# Revit family: MI-XHUB
name_source: partatom
category: Pipe Accessories
revit_build: Autodesk Revit 2018 (Build: 20170223_1515(x64)
units: mm (PartAtom-declared; Revit-internal decimal feet)

## family parameters
Always vertical = Yes
Cut with Voids When Loaded = No
Part Type = Valve - Breaks Into
Round Connector Dimension = Use Diameter
Shared = No
Work Plane-Based = No

## types (13) — shared parameters
C1 OR L1 = 0' - 3"
C2 OR L2 = 0' - 4 5/8"
C3 OR L3 = 0' - 5 7/16"
Description = Heavy Duty No Hub Coupling
Manufacturer = MIFAB
URL = www.mifab.com

## per-type parameters (varying)
| type | C4 OR L4 | Diameter_1 | Diameter_2 | Diameter_3 | Model | Option 1 | Option 2 | Option 3 | Option 4 | REDUCING DIAMETER | W |
| MI-XHUB-2 | 0' - 4" | 0' - 2" | 0' - 5" | 1' - 3" | MI-XHUB-43 | Yes | No | No | No | 0' - 2" | 0' - 0 15/32" |
| MI-XHUB-3 | 0' - 3" | 0' - 3" | 0' - 5" | 1' - 3" | MI-XHUB-3 | Yes | No | No | No | 0' - 3" | 0' - 0 15/32" |
| MI-XHUB-32 | 0' - 4" | 0' - 3" | 0' - 5" | 1' - 3" | MI-XHUB-32 | No | No | No | Yes | 0' - 2" | 0' - 0 15/32" |
| MI-XHUB-4 | 0' - 3" | 0' - 4" | 0' - 5" | 1' - 3" | MI-XHUB-4 | Yes | No | No | No | 0' - 4" | 0' - 0 9/16" |
| MI-XHUB-42 | 0' - 4" | 0' - 4" | 0' - 5" | 1' - 3" | MI-XHUB-42 | No | No | No | Yes | 0' - 2" | 0' - 0 9/16" |
| MI-XHUB-43 | 0' - 4" | 0' - 4" | 0' - 5" | 1' - 3" | MI-XHUB-43 | No | No | No | Yes | 0' - 3" | 0' - 0 15/32" |
| MI-XHUB-5 | 0' - 3" | 0' - 4" | 0' - 5" | 1' - 3" | MI-XHUB-5 | No | Yes | No | No | 0' - 3" | 0' - 0 9/16" |
| MI-XHUB-6 | 0' - 3" | 0' - 2" | 0' - 6" | 1' - 3" | MI-XHUB-6 | No | Yes | No | No | 0' - 2" | 0' - 0 9/16" |
| MI-XHUB-10 | 0' - 4 5/8" | 0' - 5" | 0' - 10" | 1' - 3" | MI-XHUB-10 | No | Yes | No | No | 0' - 2" | 0' - 0 9/16" |
| MI-XHUB-150 | 0' - 3" | 0' - 1 1/2" | 0' - 5" | 1' - 3" | MI-XHUB-150 | Yes | No | No | No | 0' - 2" | 0' - 0 9/16" |
| MI-XHUB-12 | 0' - 4 5/8" | 0' - 2" | 1' - 0" | 1' - 0" | MI-XHUB-12 | No | No | Yes | No | 0' - 2" | 0' - 0 9/16" |
| MI-XHUB-15 | 0' - 4 5/8" | 0' - 10" | 0' - 5" | 1' - 3" | MI-XHUB-15 | No | No | Yes | No | 0' - 2" | 0' - 0 9/16" |
| MI-XHUB-8 | 0' - 3" | 0' - 2" | 0' - 8" | 1' - 3" | MI-XHUB-8 | No | Yes | No | No | 0' - 2" | 0' - 0 9/16" |

## geometry (parser evidence)
native form markers: Blend x8, Sweep x23
no freeform markers — native parametric forms only
